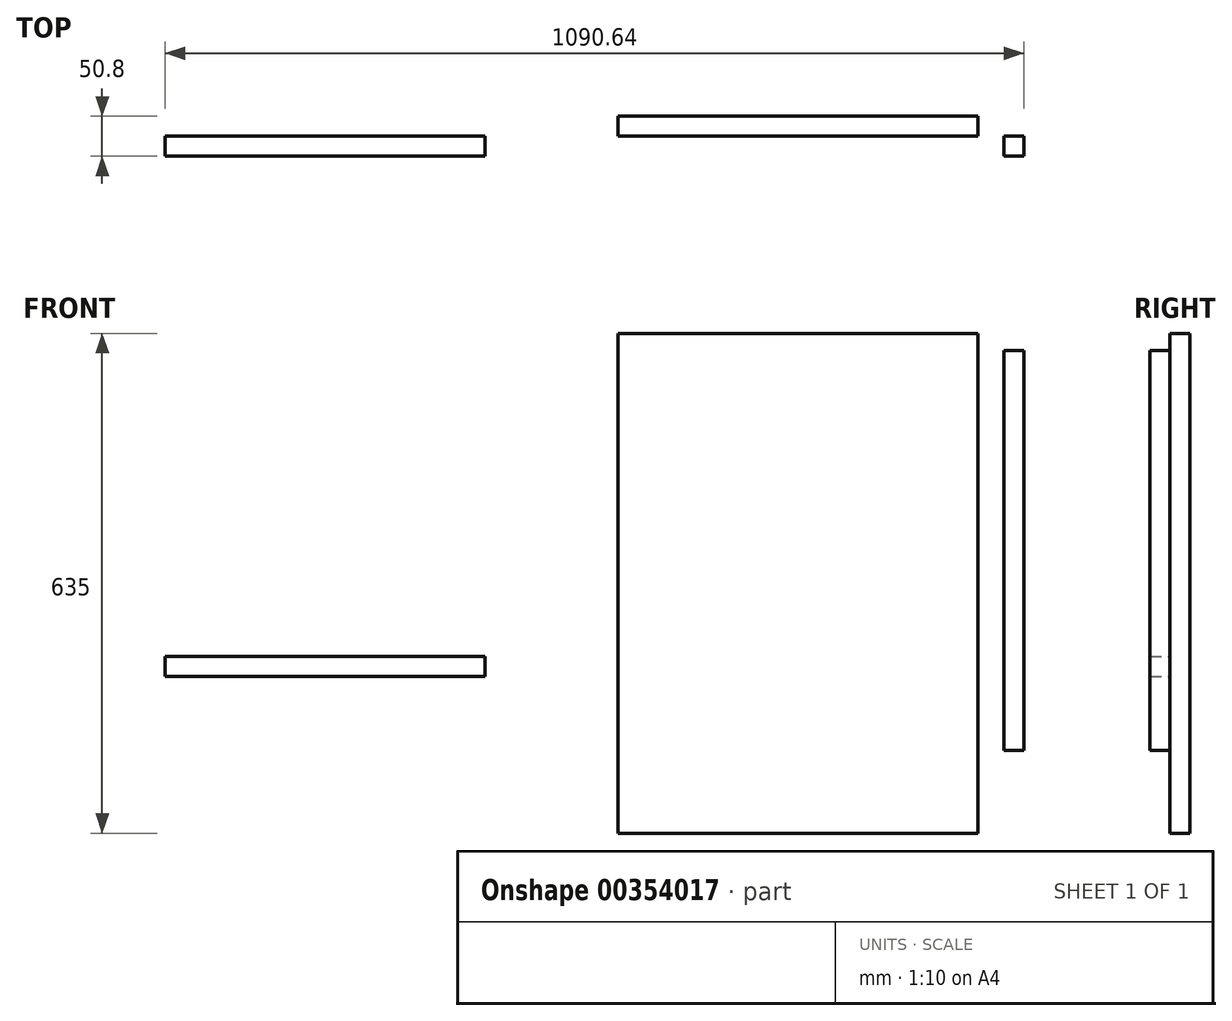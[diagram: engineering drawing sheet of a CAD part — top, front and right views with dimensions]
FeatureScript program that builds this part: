
annotation { "Feature Type Name" : "Feature", "Feature Type Description" : "" }
export const myFeature = defineFeature(function(context is Context, id is Id, definition is map)
    precondition{}
    {
        {
            var Q0;
            Q0=qCreatedBy(makeId("Front.planeOp"),FACE);
            var sketch = newSketch(context, id + "F0", { "sketchPlane" : qUnion([Q0])});
            skLineSegment(sketch, "E0", {"start": v(-36.17, 315.94) * mm, "end": v(-36.17, -319.06) * mm});
            skLineSegment(sketch, "E1", {"start": v(-36.17, -319.06) * mm, "end": v(421.03, -319.06) * mm});
            skLineSegment(sketch, "E2", {"start": v(421.03, -319.06) * mm, "end": v(421.03, 315.94) * mm});
            skLineSegment(sketch, "E3", {"start": v(421.03, 315.94) * mm, "end": v(-36.17, 315.94) * mm});
            skSolve(sketch);
        }
        {
            var Q0;
            Q0=qSketchRegion(id+"F0",true);
            extrude(context, id + "F1", {"entities" : qUnion([Q0]), "depth" : 25.4 * mm});
        }
        {
            var Q0;
            Q0=makeQuery(id+"F1.opExtrude","CAP_FACE",FACE,{"disambiguationData":[OSD([sQuery(id+"F0.wireOp",EDGE,"E0"),sQuery(id+"F0.wireOp",EDGE,"E1"),sQuery(id+"F0.wireOp",EDGE,"E2"),sQuery(id+"F0.wireOp",EDGE,"E3")])],"isStart":false});
            var sketch = newSketch(context, id + "F2", { "sketchPlane" : qUnion([Q0])});
            skLineSegment(sketch, "E4", {"start": v(453.8, 293.97) * mm, "end": v(453.8, -214.03) * mm});
            skLineSegment(sketch, "E5", {"start": v(453.8, -214.03) * mm, "end": v(479.2, -214.03) * mm});
            skLineSegment(sketch, "E6", {"start": v(479.2, -214.03) * mm, "end": v(479.2, 293.97) * mm});
            skLineSegment(sketch, "E7", {"start": v(479.2, 293.97) * mm, "end": v(453.8, 293.97) * mm});
            skSolve(sketch);
        }
        {
            var Q0;
            Q0=qSketchRegion(id+"F2",true);
            extrude(context, id + "F3", {"entities" : qUnion([Q0]), "depth" : 25.4 * mm});
        }
        {
            var Q0;
            Q0=makeQuery(id+"F1.opExtrude","CAP_FACE",FACE,{"disambiguationData":[OSD([sQuery(id+"F0.wireOp",EDGE,"E0"),sQuery(id+"F0.wireOp",EDGE,"E1"),sQuery(id+"F0.wireOp",EDGE,"E2"),sQuery(id+"F0.wireOp",EDGE,"E3")])],"isStart":false});
            var sketch = newSketch(context, id + "F4", { "sketchPlane" : qUnion([Q0])});
            skSolve(sketch);
        }
        {
            var Q0;
            Q0=makeQuery(id+"F4.imprint","IMPRINT",FACE,{"disambiguationData":[TD([[makeQuery(id+"F4.imprint","IMPRINT",EDGE,{"derivedFrom":makeQuery(id+"F1.opExtrude","CAP_EDGE",EDGE,{"disambiguationData":[OSD([sQuery(id+"F0.wireOp",EDGE,"E0")])],"isStart":false})}),1.0]])]});
            var sketch = newSketch(context, id + "F5", { "sketchPlane" : qUnion([Q0])});
            skLineSegment(sketch, "E8", {"start": v(-611.44, -119.98) * mm, "end": v(-205.04, -119.98) * mm});
            skLineSegment(sketch, "E9", {"start": v(-611.44, -119.98) * mm, "end": v(-611.44, -94.58) * mm});
            skLineSegment(sketch, "E10", {"start": v(-611.44, -94.58) * mm, "end": v(-205.04, -94.58) * mm});
            skLineSegment(sketch, "E11", {"start": v(-205.04, -94.58) * mm, "end": v(-205.04, -119.98) * mm});
            skSolve(sketch);
        }
        {
            var Q0;
            Q0=qSketchRegion(id+"F5",true);
            extrude(context, id + "F6", {"entities" : qUnion([Q0]), "depth" : 25.4 * mm});
        }
    });
